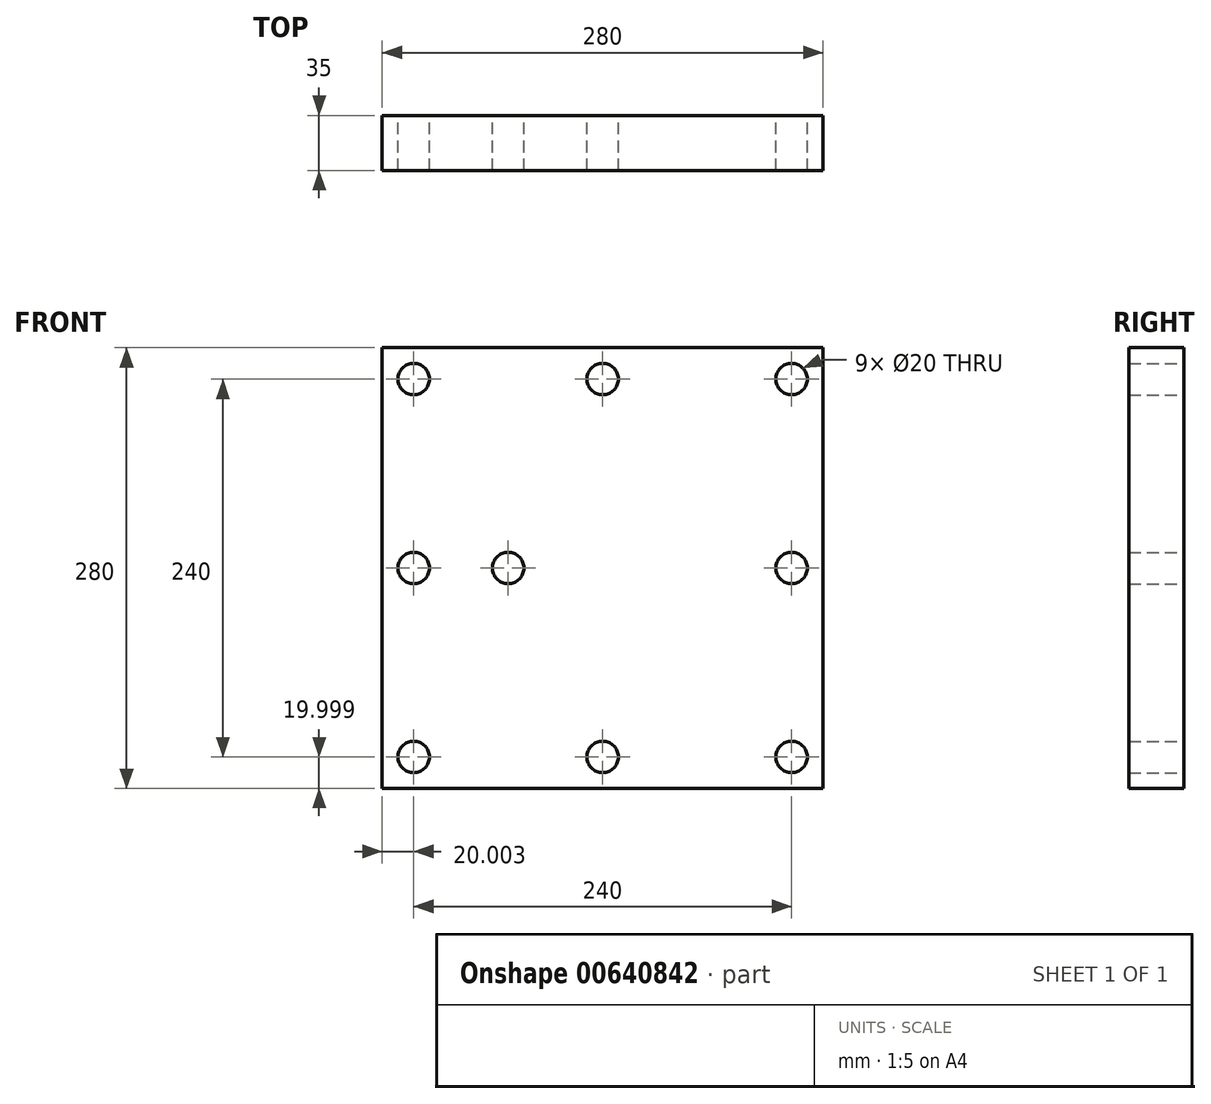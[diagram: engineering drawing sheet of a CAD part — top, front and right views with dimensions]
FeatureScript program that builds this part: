
annotation { "Feature Type Name" : "Feature", "Feature Type Description" : "" }
export const myFeature = defineFeature(function(context is Context, id is Id, definition is map)
    precondition{}
    {
        {
            var Q0;
            Q0=qCreatedBy(makeId("Front.planeOp"),FACE);
            var sketch = newSketch(context, id + "F0", { "sketchPlane" : qUnion([Q0])});
            skLineSegment(sketch, "E0.bottom", {"start": v(-162.7, 168.74) * mm, "end": v(117.3, 168.74) * mm});
            skLineSegment(sketch, "E0.top", {"start": v(-162.7, -111.26) * mm, "end": v(117.3, -111.26) * mm});
            skLineSegment(sketch, "E0.left", {"start": v(-162.7, 168.74) * mm, "end": v(-162.7, -111.26) * mm});
            skLineSegment(sketch, "E0.right", {"start": v(117.3, 168.74) * mm, "end": v(117.3, -111.26) * mm});
            skLineSegment(sketch, "E1", {"start": v(-22.7, 168.74) * mm, "end": v(-22.7, -111.26) * mm, "construction": true});
            skLineSegment(sketch, "E2", {"start": v(-162.7, 28.74) * mm, "end": v(117.3, 28.74) * mm, "construction": true});
            skLineSegment(sketch, "E3.MirrorCS", {"start": v(117.3, 28.74) * mm, "end": v(-162.7, 28.74) * mm, "construction": true});
            skPoint(sketch, "E4", {"position": v(-142.7, 148.74) * mm});
            skPoint(sketch, "E5.MirrorP", {"position": v(97.3, 148.74) * mm});
            skPoint(sketch, "E6.MirrorP", {"position": v(-142.7, -91.26) * mm});
            skPoint(sketch, "E7.MirrorP", {"position": v(97.3, -91.26) * mm});
            skPoint(sketch, "E8", {"position": v(-142.7, 28.74) * mm});
            skPoint(sketch, "E9", {"position": v(97.3, 28.74) * mm});
            skPoint(sketch, "E10", {"position": v(-22.7, -91.26) * mm});
            skPoint(sketch, "E11", {"position": v(-22.7, 148.74) * mm});
            skPoint(sketch, "E12", {"position": v(-82.7, 28.74) * mm});
            skCircle(sketch, "E13", {"center": v(-82.7, 28.74) * mm, "radius": 10 * mm});
            skPoint(sketch, "E14", {"position": v(-122.7, 28.74) * mm});
            skPoint(sketch, "E15", {"position": v(-122.7, 128.74) * mm});
            skPoint(sketch, "E16", {"position": v(77.3, 128.74) * mm});
            skPoint(sketch, "E17", {"position": v(-122.7, -71.26) * mm});
            skPoint(sketch, "E18", {"position": v(77.3, -71.26) * mm});
            skLineSegment(sketch, "E19", {"start": v(-122.7, 128.74) * mm, "end": v(-122.7, 28.74) * mm, "construction": true});
            skLineSegment(sketch, "E20", {"start": v(-122.7, 128.74) * mm, "end": v(77.3, 128.74) * mm, "construction": true});
            skLineSegment(sketch, "E21", {"start": v(77.3, 128.74) * mm, "end": v(77.3, -71.26) * mm, "construction": true});
            skLineSegment(sketch, "E22", {"start": v(-122.7, -71.26) * mm, "end": v(77.3, -71.26) * mm, "construction": true});
            skLineSegment(sketch, "E23", {"start": v(-122.7, -71.26) * mm, "end": v(-122.7, 28.74) * mm, "construction": true});
            skSolve(sketch);
        }
        {
            var Q0;
            Q0=makeQuery(id+"F0.imprint","IMPRINT",FACE,{"disambiguationData":[TD([[makeQuery(id+"F0.imprint","IMPRINT",EDGE,{"derivedFrom":sQuery(id+"F0.wireOp",EDGE,"E0.bottom")}),-1.0]])]});
            var Q1;
            Q1=makeQuery(id+"F0.imprint","IMPRINT",FACE,{"disambiguationData":[TD([[makeQuery(id+"F0.imprint","IMPRINT",EDGE,{"derivedFrom":sQuery(id+"F0.wireOp",EDGE,"48Y0K6Dc-lBbA-mTja-vAh2-u3UeNYAnCysD.bottom")}),-1.0]])]});
            extrude(context, id + "F1", {"entities" : qUnion([Q0, Q1]), "depth" : 30 * mm, "offsetDistance" : 25 * mm});
        }
        {
            var Q0;
            Q0=sQuery(id+"F0.wireOp",VERTEX,"E4");
            var Q1;
            Q1=sQuery(id+"F0.wireOp",VERTEX,"E11");
            var Q2;
            Q2=sQuery(id+"F0.wireOp",VERTEX,"E5.MirrorP");
            var Q3;
            Q3=sQuery(id+"F0.wireOp",VERTEX,"E9");
            var Q4;
            Q4=sQuery(id+"F0.wireOp",VERTEX,"E8");
            var Q5;
            Q5=sQuery(id+"F0.wireOp",VERTEX,"E6.MirrorP");
            var Q6;
            Q6=sQuery(id+"F0.wireOp",VERTEX,"E10");
            var Q7;
            Q7=sQuery(id+"F0.wireOp",VERTEX,"E7.MirrorP");
            var Q8;
            Q8=makeQuery(id+"F1.opExtrude","SWEPT_BODY",BODY,{"disambiguationData":[OSD([sQuery(id+"F0.wireOp",EDGE,"E0.bottom"),sQuery(id+"F0.wireOp",EDGE,"E0.top"),sQuery(id+"F0.wireOp",EDGE,"E0.left"),sQuery(id+"F0.wireOp",EDGE,"E0.right"),sQuery(id+"F0.wireOp",EDGE,"KUNJzKPh-e9kc-ITUx-gRbK-BSvs1wGDmoxN.bottom"),sQuery(id+"F0.wireOp",EDGE,"KUNJzKPh-e9kc-ITUx-gRbK-BSvs1wGDmoxN.top"),sQuery(id+"F0.wireOp",EDGE,"KUNJzKPh-e9kc-ITUx-gRbK-BSvs1wGDmoxN.left"),sQuery(id+"F0.wireOp",EDGE,"KUNJzKPh-e9kc-ITUx-gRbK-BSvs1wGDmoxN.right")])]});
            hole(context, id + "F2", {"style" : HoleStyle.SIMPLE, "endStyle" : HoleEndStyle.THROUGH, "oppositeDirection" : true, "holeDiameter" : 20 * mm, "majorDiameter" : 5 * mm, "isTappedThrough" : true, "tappedDepth" : 12 * mm, "tapClearance" : 3, "locations" : qUnion([Q0, Q1, Q2, Q3, Q4, Q5, Q6, Q7]), "scope" : qUnion([Q8])});
        }
        {
            var Q0;
            Q0=makeQuery(id+"F1.opExtrude","CAP_FACE",FACE,{"disambiguationData":[OSD([sQuery(id+"F0.wireOp",EDGE,"E0.bottom"),sQuery(id+"F0.wireOp",EDGE,"E0.top"),sQuery(id+"F0.wireOp",EDGE,"E0.left"),sQuery(id+"F0.wireOp",EDGE,"E0.right"),sQuery(id+"F0.wireOp",EDGE,"E13"),sQuery(id+"F0.wireOp",EDGE,"ffzkFZV3-GkbH-DqvR-crvG-u3uyopuF3Fic"),sQuery(id+"F0.wireOp",EDGE,"kKkt2ole-RwbE-acCZ-x2Oi-StLxR2WInH8C"),sQuery(id+"F0.wireOp",EDGE,"22VrOk4a-a4WO-e7FK-K8u0-mu7Y5IIvOiv6"),sQuery(id+"F0.wireOp",EDGE,"32d0ee91-9273-4300-8955-c9796f1cdee52.MirrorC"),sQuery(id+"F0.wireOp",EDGE,"32d0ee91-9273-4300-8955-c9796f1cdee53.MirrorC")])],"isStart":false});
            var sketch = newSketch(context, id + "F3", { "sketchPlane" : qUnion([Q0])});
            skLineSegment(sketch, "E24.bottom", {"start": v(-162.7, 168.74) * mm, "end": v(117.3, 168.74) * mm});
            skLineSegment(sketch, "E24.top", {"start": v(-162.7, -111.26) * mm, "end": v(117.3, -111.26) * mm});
            skLineSegment(sketch, "E24.left", {"start": v(-162.7, 168.74) * mm, "end": v(-162.7, -111.26) * mm});
            skLineSegment(sketch, "E24.right", {"start": v(117.3, 168.74) * mm, "end": v(117.3, -111.26) * mm});
            skSolve(sketch);
        }
        {
            var Q0;
            Q0=makeQuery(id+"F3.imprint","IMPRINT",FACE,{"disambiguationData":[TD([[makeQuery(id+"F3.imprint","IMPRINT",EDGE,{"derivedFrom":sQuery(id+"F3.wireOp",EDGE,"E24.bottom")}),-1.0]])]});
            extrude(context, id + "F4", {"entities" : qUnion([Q0]), "operationType" : NewBodyOperationType.ADD, "depth" : 5 * mm, "offsetDistance" : 25 * mm});
        }
    });
